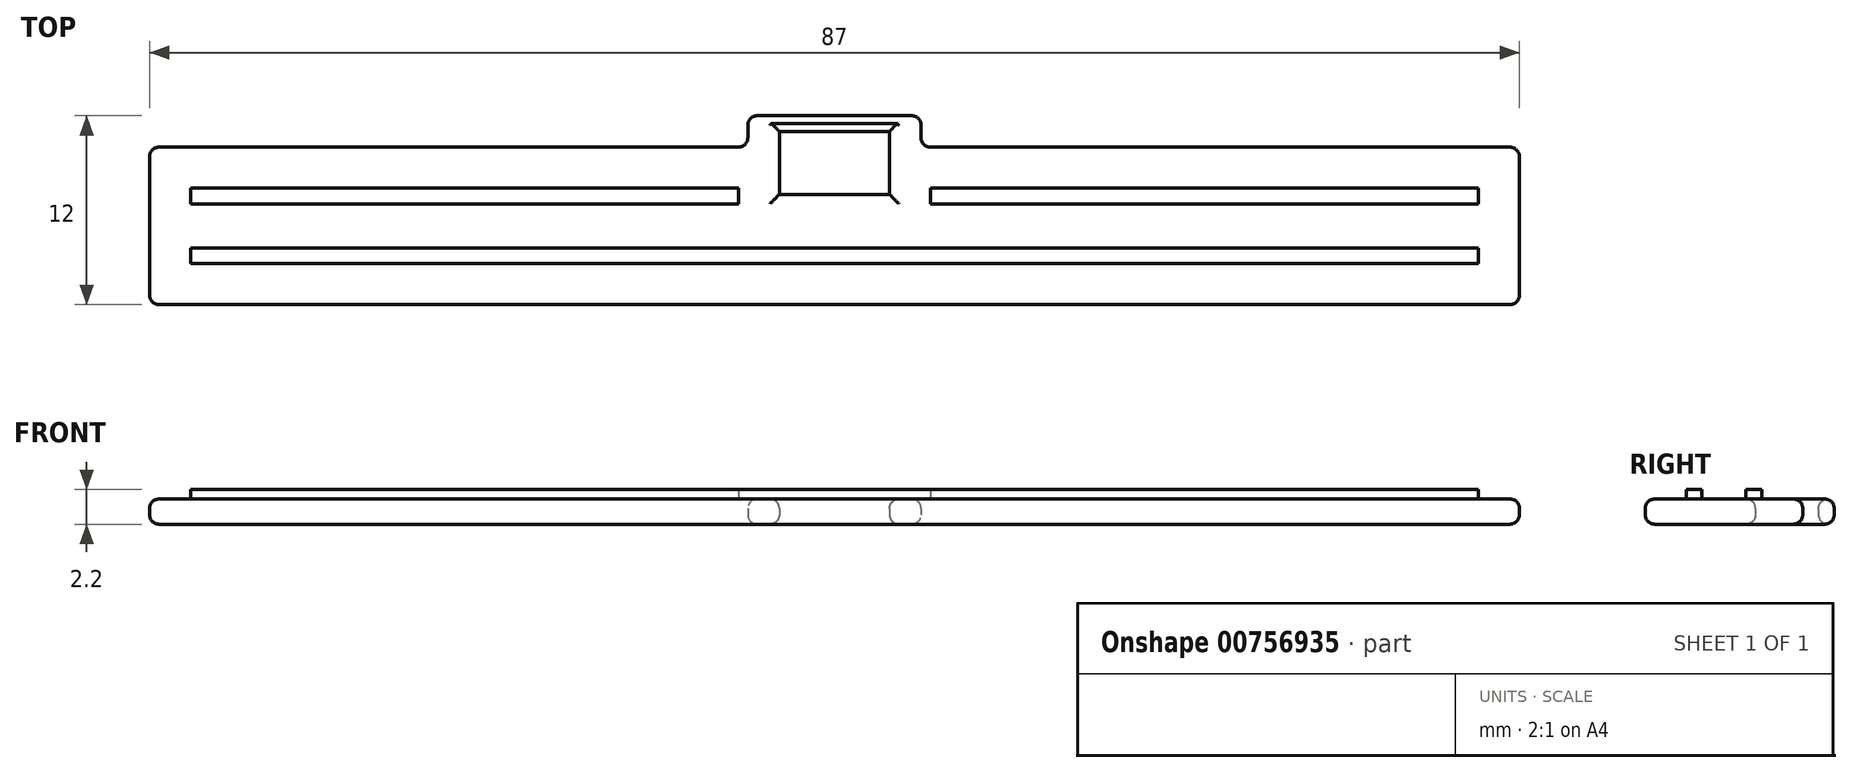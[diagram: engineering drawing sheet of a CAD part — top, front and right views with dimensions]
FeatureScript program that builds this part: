
annotation { "Feature Type Name" : "Feature", "Feature Type Description" : "" }
export const myFeature = defineFeature(function(context is Context, id is Id, definition is map)
    precondition{}
    {
        {
            var Q0;
            Q0=qCreatedBy(makeId("Top.planeOp"),FACE);
            var sketch = newSketch(context, id + "F0", { "sketchPlane" : qUnion([Q0])});
            skLineSegment(sketch, "E0", {"start": v(-43.5, 0) * mm, "end": v(43.5, 0) * mm});
            skLineSegment(sketch, "E1", {"start": v(43.5, 0) * mm, "end": v(43.5, 10) * mm});
            skLineSegment(sketch, "E2", {"start": v(43.5, 10) * mm, "end": v(5.5, 10) * mm});
            skLineSegment(sketch, "E3", {"start": v(5.5, 10) * mm, "end": v(5.5, 12) * mm});
            skLineSegment(sketch, "E4", {"start": v(5.5, 12) * mm, "end": v(-5.5, 12) * mm});
            skLineSegment(sketch, "E5", {"start": v(-5.5, 12) * mm, "end": v(-5.5, 10) * mm});
            skLineSegment(sketch, "E6", {"start": v(-5.5, 10) * mm, "end": v(-43.5, 10) * mm});
            skLineSegment(sketch, "E7", {"start": v(-43.5, 10) * mm, "end": v(-43.5, 0) * mm});
            skLineSegment(sketch, "E8", {"start": v(-3.5, 11) * mm, "end": v(-3.5, 7) * mm});
            skLineSegment(sketch, "E9", {"start": v(-3.5, 7) * mm, "end": v(3.5, 7) * mm});
            skLineSegment(sketch, "E10", {"start": v(3.5, 7) * mm, "end": v(3.5, 11) * mm});
            skLineSegment(sketch, "E11", {"start": v(3.5, 11) * mm, "end": v(-3.5, 11) * mm});
            skSolve(sketch);
        }
        {
            var Q0;
            Q0=makeQuery(id+"F0.imprint","IMPRINT",FACE,{"disambiguationData":[TD([[makeQuery(id+"F0.imprint","IMPRINT",EDGE,{"derivedFrom":sQuery(id+"F0.wireOp",EDGE,"E0")}),1.0]])]});
            extrude(context, id + "F1", {"entities" : qUnion([Q0]), "depth" : 1.6 * mm, "offsetDistance" : 25 * mm});
        }
        {
            var Q0;
            Q0=makeQuery(id+"F1.opExtrude","CAP_EDGE",EDGE,{"disambiguationData":[OSD([sQuery(id+"F0.wireOp",EDGE,"E7")])],"isStart":false});
            var Q1;
            Q1=makeQuery(id+"F1.opExtrude","CAP_FACE",FACE,{"disambiguationData":[OSD([sQuery(id+"F0.wireOp",EDGE,"E0"),sQuery(id+"F0.wireOp",EDGE,"E1"),sQuery(id+"F0.wireOp",EDGE,"E2"),sQuery(id+"F0.wireOp",EDGE,"E3"),sQuery(id+"F0.wireOp",EDGE,"E4"),sQuery(id+"F0.wireOp",EDGE,"E5"),sQuery(id+"F0.wireOp",EDGE,"E6"),sQuery(id+"F0.wireOp",EDGE,"E7"),sQuery(id+"F0.wireOp",EDGE,"E8"),sQuery(id+"F0.wireOp",EDGE,"E9"),sQuery(id+"F0.wireOp",EDGE,"E10"),sQuery(id+"F0.wireOp",EDGE,"E11")])],"isStart":false});
            var Q2;
            Q2=makeQuery(id+"F1.opExtrude","CAP_FACE",FACE,{"disambiguationData":[OSD([sQuery(id+"F0.wireOp",EDGE,"E0"),sQuery(id+"F0.wireOp",EDGE,"E1"),sQuery(id+"F0.wireOp",EDGE,"E2"),sQuery(id+"F0.wireOp",EDGE,"E3"),sQuery(id+"F0.wireOp",EDGE,"E4"),sQuery(id+"F0.wireOp",EDGE,"E5"),sQuery(id+"F0.wireOp",EDGE,"E6"),sQuery(id+"F0.wireOp",EDGE,"E7"),sQuery(id+"F0.wireOp",EDGE,"E8"),sQuery(id+"F0.wireOp",EDGE,"E9"),sQuery(id+"F0.wireOp",EDGE,"E10"),sQuery(id+"F0.wireOp",EDGE,"E11")])],"isStart":true});
            var Q3;
            Q3=makeQuery(id+"F1.opExtrude","SWEPT_EDGE",EDGE,{"disambiguationData":[OSD([sQuery(id+"F0.wireOp",EDGE,"E0"),sQuery(id+"F0.wireOp",EDGE,"E1")])]});
            var Q4;
            Q4=makeQuery(id+"F1.opExtrude","SWEPT_EDGE",EDGE,{"disambiguationData":[OSD([sQuery(id+"F0.wireOp",EDGE,"E1"),sQuery(id+"F0.wireOp",EDGE,"E2")])]});
            var Q5;
            Q5=makeQuery(id+"F1.opExtrude","SWEPT_EDGE",EDGE,{"disambiguationData":[OSD([sQuery(id+"F0.wireOp",EDGE,"E2"),sQuery(id+"F0.wireOp",EDGE,"E3")])]});
            var Q6;
            Q6=makeQuery(id+"F1.opExtrude","SWEPT_EDGE",EDGE,{"disambiguationData":[OSD([sQuery(id+"F0.wireOp",EDGE,"E3"),sQuery(id+"F0.wireOp",EDGE,"E4")])]});
            var Q7;
            Q7=makeQuery(id+"F1.opExtrude","SWEPT_EDGE",EDGE,{"disambiguationData":[OSD([sQuery(id+"F0.wireOp",EDGE,"E4"),sQuery(id+"F0.wireOp",EDGE,"E5")])]});
            var Q8;
            Q8=makeQuery(id+"F1.opExtrude","SWEPT_EDGE",EDGE,{"disambiguationData":[OSD([sQuery(id+"F0.wireOp",EDGE,"E5"),sQuery(id+"F0.wireOp",EDGE,"E6")])]});
            var Q9;
            Q9=makeQuery(id+"F1.opExtrude","SWEPT_EDGE",EDGE,{"disambiguationData":[OSD([sQuery(id+"F0.wireOp",EDGE,"E6"),sQuery(id+"F0.wireOp",EDGE,"E7")])]});
            var Q10;
            Q10=makeQuery(id+"F1.opExtrude","SWEPT_EDGE",EDGE,{"disambiguationData":[OSD([sQuery(id+"F0.wireOp",EDGE,"E0"),sQuery(id+"F0.wireOp",EDGE,"E7")])]});
            fillet(context, id + "F2", {"entities" : qUnion([Q0, Q1, Q2, Q3, Q4, Q5, Q6, Q7, Q8, Q9, Q10]), "radius" : .6 * mm, "tangentPropagation" : true, "allowEdgeOverflow" : false});
        }
        {
            var Q0;
            Q0=qCreatedBy(makeId("Top.planeOp"),FACE);
            var sketch = newSketch(context, id + "F3", { "sketchPlane" : qUnion([Q0])});
            skLineSegment(sketch, "E12.bottom", {"start": v(-40.9, 7.4) * mm, "end": v(-6.1, 7.4) * mm});
            skLineSegment(sketch, "E12.top", {"start": v(-40.9, 6.4) * mm, "end": v(-6.1, 6.4) * mm});
            skLineSegment(sketch, "E12.left", {"start": v(-40.9, 7.4) * mm, "end": v(-40.9, 6.4) * mm});
            skLineSegment(sketch, "E12.right", {"start": v(-6.1, 7.4) * mm, "end": v(-6.1, 6.4) * mm});
            skLineSegment(sketch, "E13.bottom", {"start": v(-40.9, 3.6) * mm, "end": v(40.9, 3.6) * mm});
            skLineSegment(sketch, "E13.top", {"start": v(-40.9, 2.6) * mm, "end": v(40.9, 2.6) * mm});
            skLineSegment(sketch, "E13.left", {"start": v(-40.9, 3.6) * mm, "end": v(-40.9, 2.6) * mm});
            skLineSegment(sketch, "E13.right", {"start": v(40.9, 3.6) * mm, "end": v(40.9, 2.6) * mm});
            skLineSegment(sketch, "E14.bottom", {"start": v(6.1, 7.4) * mm, "end": v(40.9, 7.4) * mm});
            skLineSegment(sketch, "E14.top", {"start": v(6.1, 6.4) * mm, "end": v(40.9, 6.4) * mm});
            skLineSegment(sketch, "E14.left", {"start": v(6.1, 7.4) * mm, "end": v(6.1, 6.4) * mm});
            skLineSegment(sketch, "E14.right", {"start": v(40.9, 7.4) * mm, "end": v(40.9, 6.4) * mm});
            skLineSegment(sketch, "E15", {"start": v(-40.9, 6.4) * mm, "end": v(-40.9, 3.6) * mm});
            skLineSegment(sketch, "E16", {"start": v(40.9, 6.4) * mm, "end": v(40.9, 3.6) * mm});
            skSolve(sketch);
        }
        {
            var Q0;
            Q0 = qSketchRegion(id + "F3", true);
            extrude(context, id + "F4", {"entities" : qUnion([Q0]), "operationType" : NewBodyOperationType.ADD, "depth" : 2.2 * mm, "offsetDistance" : 25 * mm});
        }
    });
